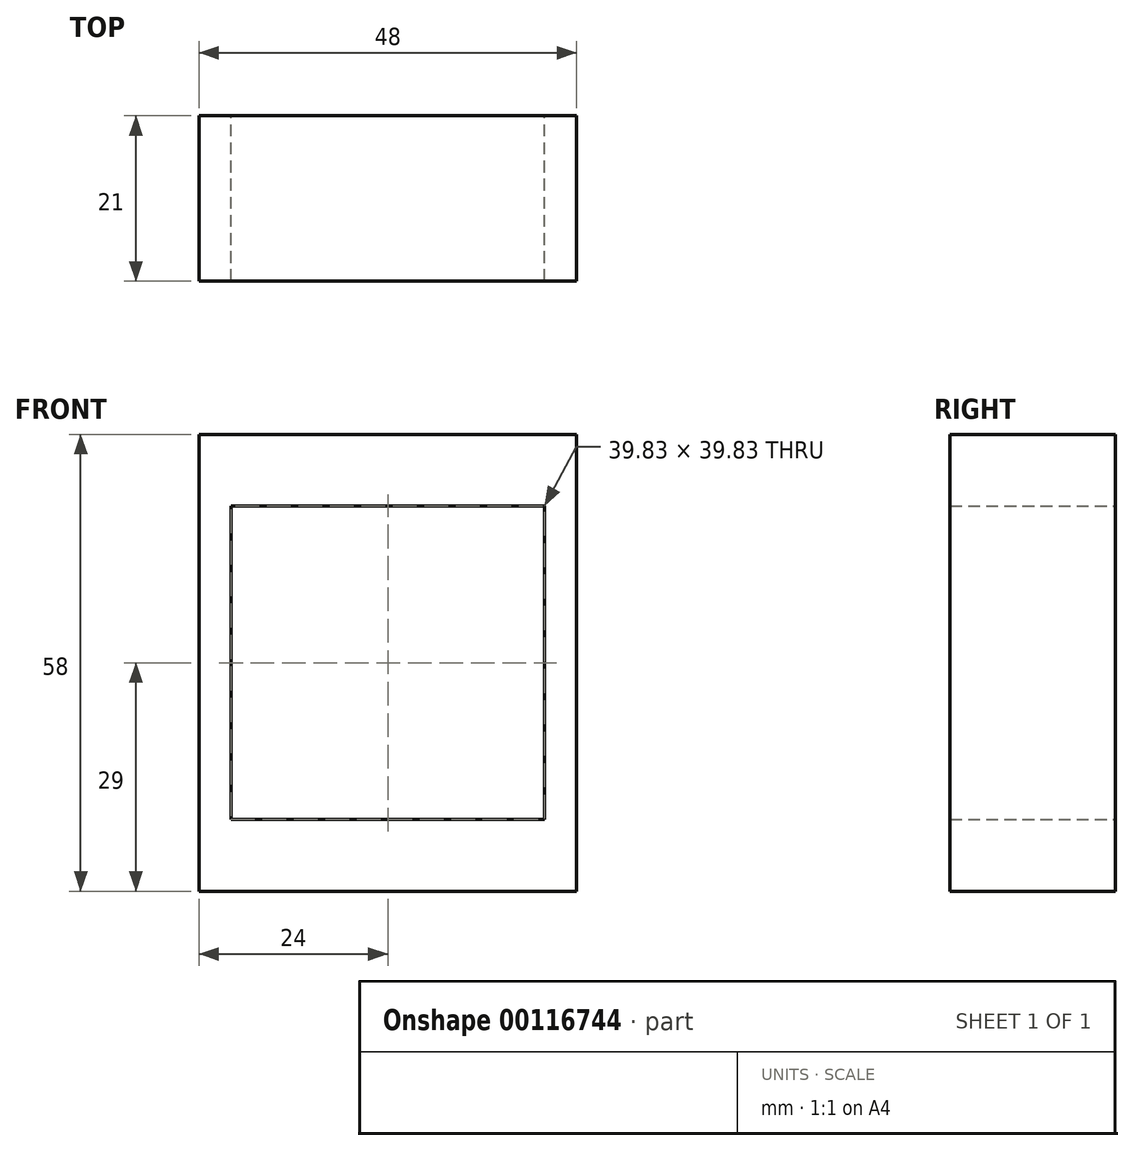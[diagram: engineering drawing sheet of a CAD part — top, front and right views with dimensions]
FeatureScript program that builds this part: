
annotation { "Feature Type Name" : "Feature", "Feature Type Description" : "" }
export const myFeature = defineFeature(function(context is Context, id is Id, definition is map)
    precondition{}
    {
        {
            var Q0;
            Q0=qCreatedBy(makeId("Front.planeOp"),FACE);
            var sketch = newSketch(context, id + "F0", { "sketchPlane" : qUnion([Q0])});
            skLineSegment(sketch, "E0.bottom", {"start": v(24, 29) * mm, "end": v(-24, 29) * mm});
            skLineSegment(sketch, "E0.top", {"start": v(24, -29) * mm, "end": v(-24, -29) * mm});
            skLineSegment(sketch, "E0.left", {"start": v(24, 29) * mm, "end": v(24, -29) * mm});
            skLineSegment(sketch, "E0.right", {"start": v(-24, 29) * mm, "end": v(-24, -29) * mm});
            skPoint(sketch, "E0.middle", {"position": v(0, 0) * mm});
            skLineSegment(sketch, "E1.bottom", {"start": v(19.92, 19.92) * mm, "end": v(-19.92, 19.92) * mm});
            skLineSegment(sketch, "E1.top", {"start": v(19.92, -19.92) * mm, "end": v(-19.92, -19.92) * mm});
            skLineSegment(sketch, "E1.left", {"start": v(19.92, 19.92) * mm, "end": v(19.92, -19.92) * mm});
            skLineSegment(sketch, "E1.right", {"start": v(-19.92, 19.92) * mm, "end": v(-19.92, -19.92) * mm});
            skSolve(sketch);
        }
        {
            var Q0;
            Q0 = qSketchRegion(id + "F0", true);
            extrude(context, id + "F1", {"entities" : qUnion([Q0]), "depth" : 21 * mm});
        }
    });
